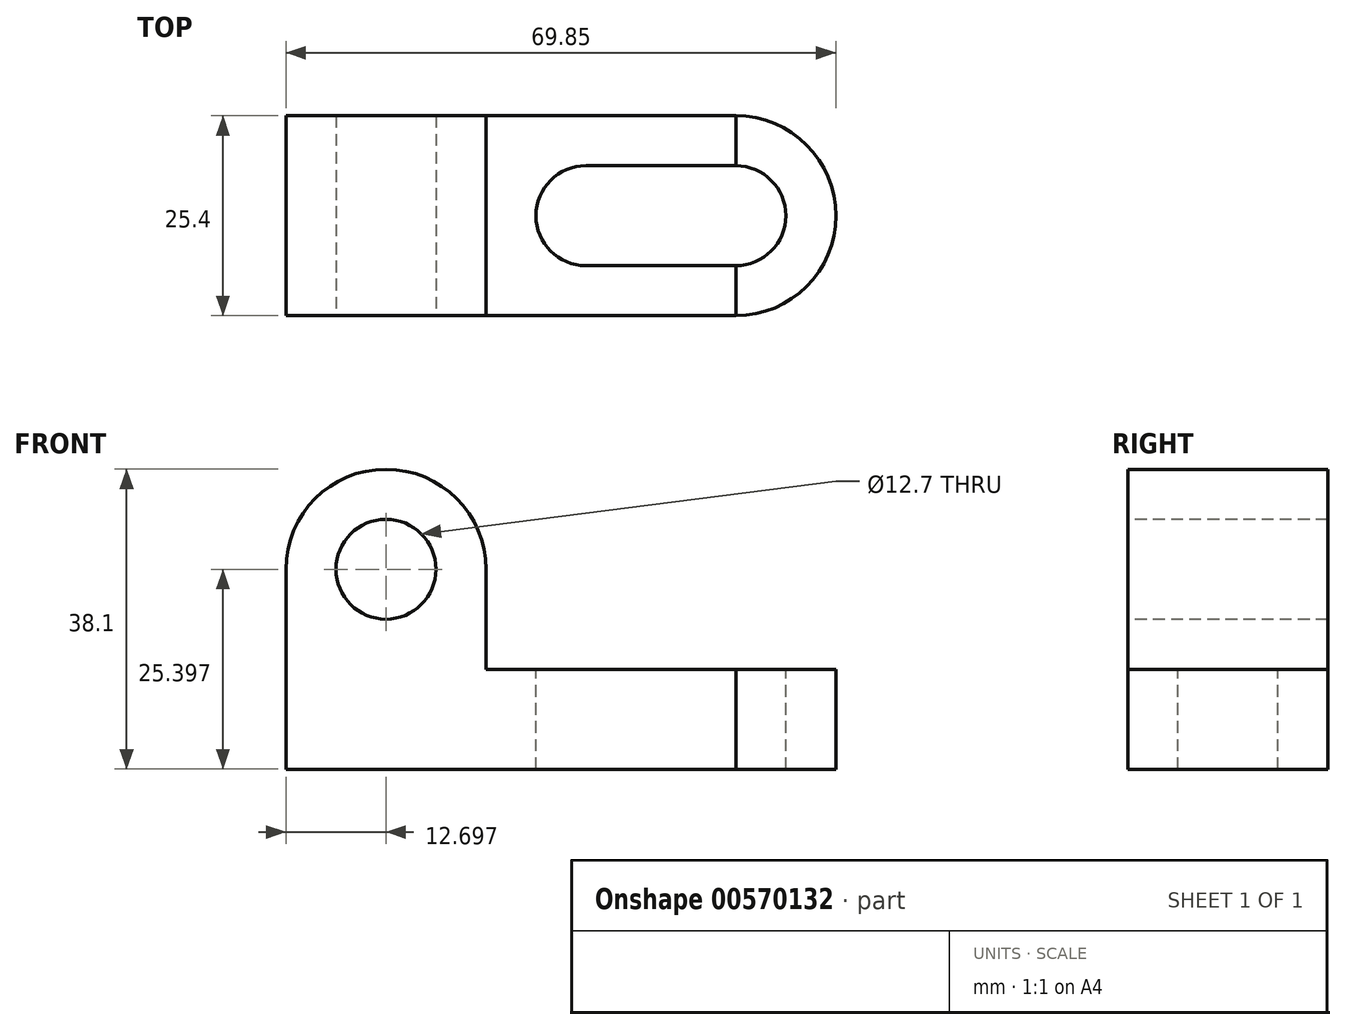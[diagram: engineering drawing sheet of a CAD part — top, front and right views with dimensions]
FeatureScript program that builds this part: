
annotation { "Feature Type Name" : "Feature", "Feature Type Description" : "" }
export const myFeature = defineFeature(function(context is Context, id is Id, definition is map)
    precondition{}
    {
        {
            var Q0;
            Q0=qCreatedBy(makeId("Front.planeOp"),FACE);
            var sketch = newSketch(context, id + "F0", { "sketchPlane" : qUnion([Q0])});
            skLineSegment(sketch, "E0", {"start": v(-82.94, 36.48) * mm, "end": v(-82.94, 11.08) * mm});
            skLineSegment(sketch, "E1", {"start": v(-82.94, 11.08) * mm, "end": v(-25.8, 11.08) * mm});
            skLineSegment(sketch, "E2", {"start": v(-25.8, 11.08) * mm, "end": v(-25.8, 23.78) * mm});
            skLineSegment(sketch, "E3", {"start": v(-25.8, 23.78) * mm, "end": v(-57.54, 23.78) * mm});
            skLineSegment(sketch, "E4", {"start": v(-57.54, 23.78) * mm, "end": v(-57.54, 36.48) * mm});
            skLineSegment(sketch, "E5", {"start": v(-57.54, 36.48) * mm, "end": v(-82.94, 36.48) * mm});
            skArc(sketch, "E6", {"start": v(-57.54, 36.48) * mm, "mid": v(-70.24, 49.18) * mm, "end": v(-82.94, 36.48) * mm});
            skLineSegment(sketch, "E7", {"start": v(-70.24, 49.18) * mm, "end": v(-70.24, 36.48) * mm});
            skSolve(sketch);
        }
        {
            var Q0;
            {var subQ0=sQuery(id+"F0.wireOp",EDGE,"E0");Q0=makeQuery(id+"F0.imprint","IMPRINT",FACE,{"disambiguationData":[TD([[makeQuery(id+"F0.imprint","IMPRINT",EDGE,{"derivedFrom":subQ0}),1.0]])]});}
            var Q1;
            {var subQ3=sQuery(id+"F0.wireOp",EDGE,"E7");Q1=makeQuery(id+"F0.imprint","IMPRINT",FACE,{"disambiguationData":[TD([[makeQuery(id+"F0.imprint","IMPRINT",EDGE,{"derivedFrom":subQ3}),1.0]])]});}
            var Q2;
            {var subQ3=sQuery(id+"F0.wireOp",EDGE,"E7");Q2=makeQuery(id+"F0.imprint","IMPRINT",FACE,{"disambiguationData":[TD([[makeQuery(id+"F0.imprint","IMPRINT",EDGE,{"derivedFrom":subQ3}),-1.0]])]});}
            extrude(context, id + "F1", {"entities" : qUnion([Q0, Q1, Q2]), "depth" : 25.4 * mm, "offsetDistance" : 25.4 * mm});
        }
        {
            var Q0;
            Q0=makeQuery(id+"F1.opExtrude","SWEPT_FACE",FACE,{"disambiguationData":[OSD([sQuery(id+"F0.wireOp",EDGE,"E3")])]});
            var sketch = newSketch(context, id + "F2", { "sketchPlane" : qUnion([Q0])});
            skArc(sketch, "E8", {"start": v(-25.8, -25.4) * mm, "mid": v(-13.1, -12.7) * mm, "end": v(-25.8, 0) * mm});
            skLineSegment(sketch, "E9", {"start": v(-25.8, -12.7) * mm, "end": v(-13.1, -12.7) * mm});
            skSolve(sketch);
        }
        {
            var Q0;
            {var subQ4=sQuery(id+"F2.wireOp",EDGE,"E9");Q0=makeQuery(id+"F2.imprint","IMPRINT",FACE,{"disambiguationData":[TD([[makeQuery(id+"F2.imprint","IMPRINT",EDGE,{"derivedFrom":subQ4}),1.0]])]});}
            var Q1;
            {var subQ4=sQuery(id+"F2.wireOp",EDGE,"E9");Q1=makeQuery(id+"F2.imprint","IMPRINT",FACE,{"disambiguationData":[TD([[makeQuery(id+"F2.imprint","IMPRINT",EDGE,{"derivedFrom":subQ4}),-1.0]])]});}
            extrude(context, id + "F3", {"entities" : qUnion([Q0, Q1]), "oppositeDirection" : true, "depth" : 12.7 * mm, "offsetDistance" : 25.4 * mm});
        }
        {
            var Q0;
            Q0=makeQuery(id+"F1.opExtrude","CAP_FACE",FACE,{"disambiguationData":[OSD([sQuery(id+"F0.wireOp",EDGE,"E0"),sQuery(id+"F0.wireOp",EDGE,"E1"),sQuery(id+"F0.wireOp",EDGE,"E2"),sQuery(id+"F0.wireOp",EDGE,"E3"),sQuery(id+"F0.wireOp",EDGE,"E4"),sQuery(id+"F0.wireOp",EDGE,"E6")])],"isStart":false});
            var sketch = newSketch(context, id + "F4", { "sketchPlane" : qUnion([Q0])});
            skCircle(sketch, "E10", {"center": v(-70.24, 36.48) * mm, "radius": 6.35 * mm});
            skSolve(sketch);
        }
        {
            var Q0;
            Q0=sQuery(id+"F4.wireOp",VERTEX,"E10.center");
            var Q1;
            Q1=makeQuery(id+"F1.opExtrude","SWEPT_BODY",BODY,{"disambiguationData":[OSD([sQuery(id+"F0.wireOp",EDGE,"E0"),sQuery(id+"F0.wireOp",EDGE,"E1"),sQuery(id+"F0.wireOp",EDGE,"E2"),sQuery(id+"F0.wireOp",EDGE,"E3"),sQuery(id+"F0.wireOp",EDGE,"E4"),sQuery(id+"F0.wireOp",EDGE,"E6")])]});
            hole(context, id + "F5", {"style" : HoleStyle.SIMPLE, "endStyle" : HoleEndStyle.THROUGH, "holeDiameter" : 12.7 * mm, "isTappedThrough" : true, "tappedDepth" : 12.7 * mm, "tapClearance" : 3, "locations" : qUnion([Q0]), "scope" : qUnion([Q1])});
        }
        {
            var Q0;
            Q0=makeQuery(id+"F1.opExtrude","SWEPT_FACE",FACE,{"disambiguationData":[OSD([sQuery(id+"F0.wireOp",EDGE,"E3")])]});
            var sketch = newSketch(context, id + "F6", { "sketchPlane" : qUnion([Q0])});
            skLineSegment(sketch, "E11", {"start": v(-44.84, -6.35) * mm, "end": v(-44.84, -19.05) * mm});
            skLineSegment(sketch, "E12", {"start": v(-44.84, -19.05) * mm, "end": v(-25.8, -19.05) * mm});
            skLineSegment(sketch, "E13", {"start": v(-25.8, -19.05) * mm, "end": v(-25.8, -6.35) * mm});
            skLineSegment(sketch, "E14", {"start": v(-25.8, -6.35) * mm, "end": v(-44.84, -6.35) * mm});
            skArc(sketch, "E15", {"start": v(-25.8, -19.05) * mm, "mid": v(-19.44, -12.7) * mm, "end": v(-25.8, -6.35) * mm});
            skArc(sketch, "E16", {"start": v(-44.84, -6.35) * mm, "mid": v(-51.2, -12.7) * mm, "end": v(-44.84, -19.05) * mm});
            skSolve(sketch);
        }
        {
            var Q0;
            Q0=makeQuery(id+"F6.imprint","IMPRINT",FACE,{"disambiguationData":[TD([[makeQuery(id+"F6.imprint","IMPRINT",EDGE,{"derivedFrom":sQuery(id+"F6.wireOp",EDGE,"E13")}),-1.0]])]});
            var Q1;
            Q1=makeQuery(id+"F6.imprint","IMPRINT",FACE,{"disambiguationData":[TD([[makeQuery(id+"F6.imprint","IMPRINT",EDGE,{"derivedFrom":sQuery(id+"F6.wireOp",EDGE,"E11")}),1.0]])]});
            var Q2;
            Q2=makeQuery(id+"F6.imprint","IMPRINT",FACE,{"disambiguationData":[TD([[makeQuery(id+"F6.imprint","IMPRINT",EDGE,{"derivedFrom":sQuery(id+"F6.wireOp",EDGE,"E11")}),-1.0]])]});
            extrude(context, id + "F7", {"entities" : qUnion([Q0, Q1, Q2]), "operationType" : NewBodyOperationType.REMOVE, "oppositeDirection" : true, "depth" : 25.4 * mm, "offsetDistance" : 25.4 * mm});
        }
    });
